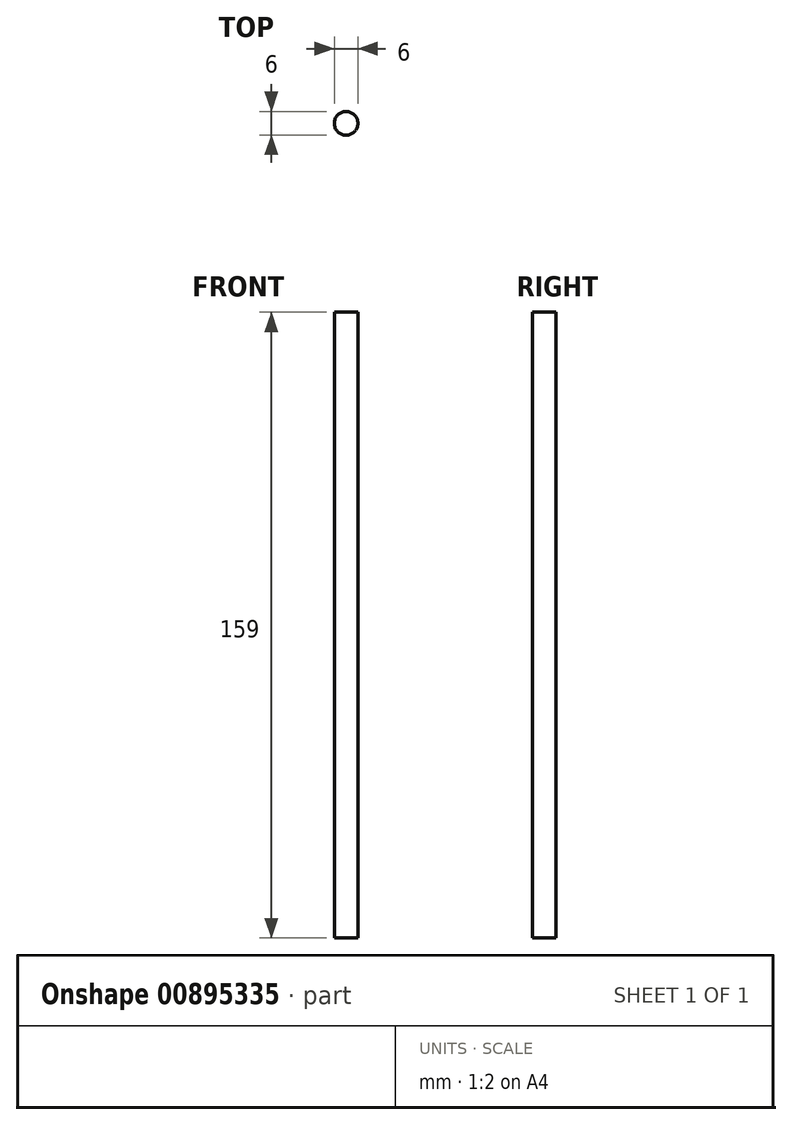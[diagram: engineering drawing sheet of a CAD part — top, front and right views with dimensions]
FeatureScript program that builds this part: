
annotation { "Feature Type Name" : "Feature", "Feature Type Description" : "" }
export const myFeature = defineFeature(function(context is Context, id is Id, definition is map)
    precondition{}
    {
        {
            var Q0;
            Q0=qCreatedBy(makeId("Top.planeOp"),FACE);
            var sketch = newSketch(context, id + "F0", { "sketchPlane" : qUnion([Q0])});
            skCircle(sketch, "E0", {"center": v(0, 0) * mm, "radius": 3 * mm});
            skSolve(sketch);
        }
        {
            var Q0;
            Q0 = qSketchRegion(id + "F0", true);
            extrude(context, id + "F1", {"entities" : qUnion([Q0]), "depth" : 159 * mm, "offsetDistance" : 25 * mm});
        }
    });
